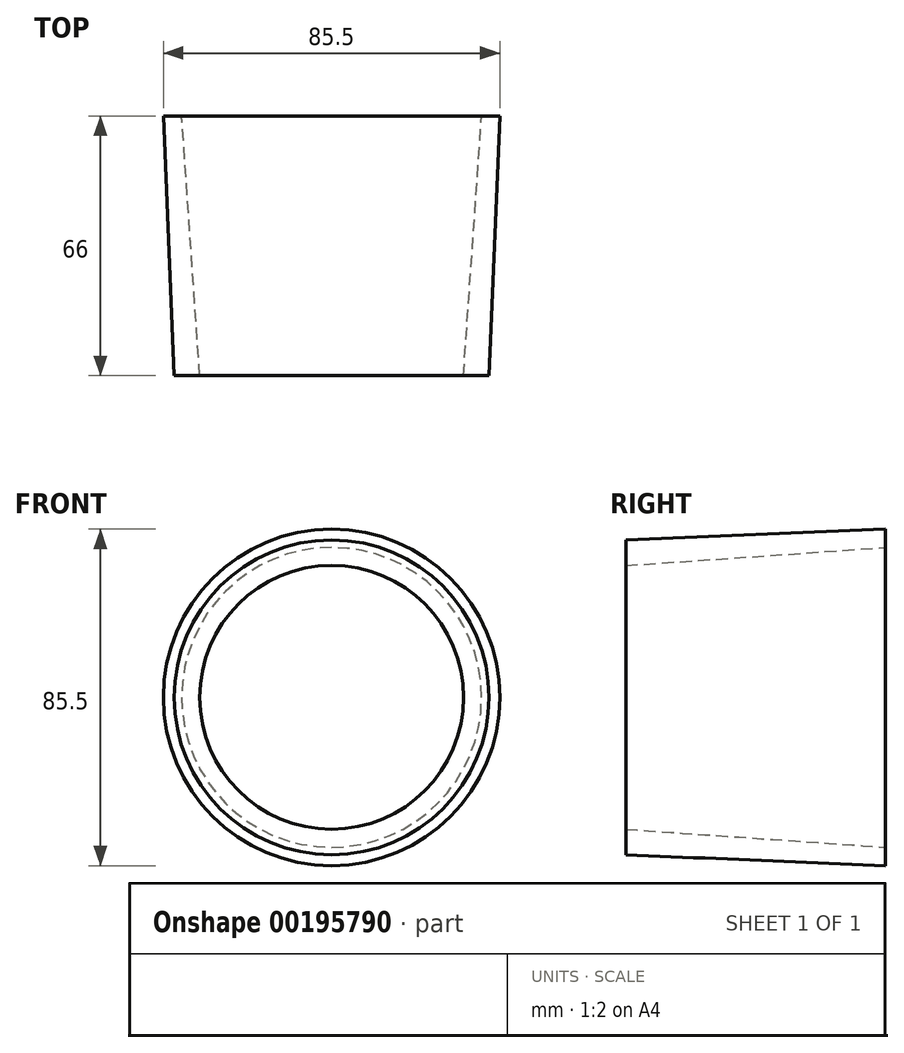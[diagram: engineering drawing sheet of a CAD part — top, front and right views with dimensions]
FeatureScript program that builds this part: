
annotation { "Feature Type Name" : "Feature", "Feature Type Description" : "" }
export const myFeature = defineFeature(function(context is Context, id is Id, definition is map)
    precondition{}
    {
        {
            var Q0;
            Q0=qCreatedBy(makeId("Top.planeOp"),FACE);
            var sketch = newSketch(context, id + "F0", { "sketchPlane" : qUnion([Q0])});
            skLineSegment(sketch, "E0", {"start": v(-41.5, 36) * mm, "end": v(-40, 0) * mm});
            skLineSegment(sketch, "E1", {"start": v(-40, 0) * mm, "end": v(-33.5, 0) * mm});
            skLineSegment(sketch, "E2", {"start": v(-33.5, 0) * mm, "end": v(-36, 36) * mm});
            skLineSegment(sketch, "E3", {"start": v(-36, 36) * mm, "end": v(-41.5, 36) * mm, "construction": true});
            skLineSegment(sketch, "E4", {"start": v(0, 0) * mm, "end": v(0, 21.64) * mm, "construction": true});
            skLineSegment(sketch, "E5", {"start": v(-41.5, 36) * mm, "end": v(-42.75, 66) * mm});
            skLineSegment(sketch, "E6", {"start": v(-42.75, 66) * mm, "end": v(-38.08, 66) * mm});
            skLineSegment(sketch, "E7", {"start": v(-38.08, 66) * mm, "end": v(-36, 36) * mm});
            skSolve(sketch);
        }
        {
            var Q0;
            Q0=makeQuery(id+"F0.imprint","IMPRINT",FACE,{"disambiguationData":[TD([[makeQuery(id+"F0.imprint","IMPRINT",EDGE,{"derivedFrom":sQuery(id+"F0.wireOp",EDGE,"E0")}),1.0]])]});
            var Q1;
            Q1=sQuery(id+"F0.wireOp",EDGE,"E4");
            revolve(context, id + "F1", {"entities" : qUnion([Q0]), "axis" : qUnion([Q1]), "revolveType" : RevolveType.FULL});
        }
    });
